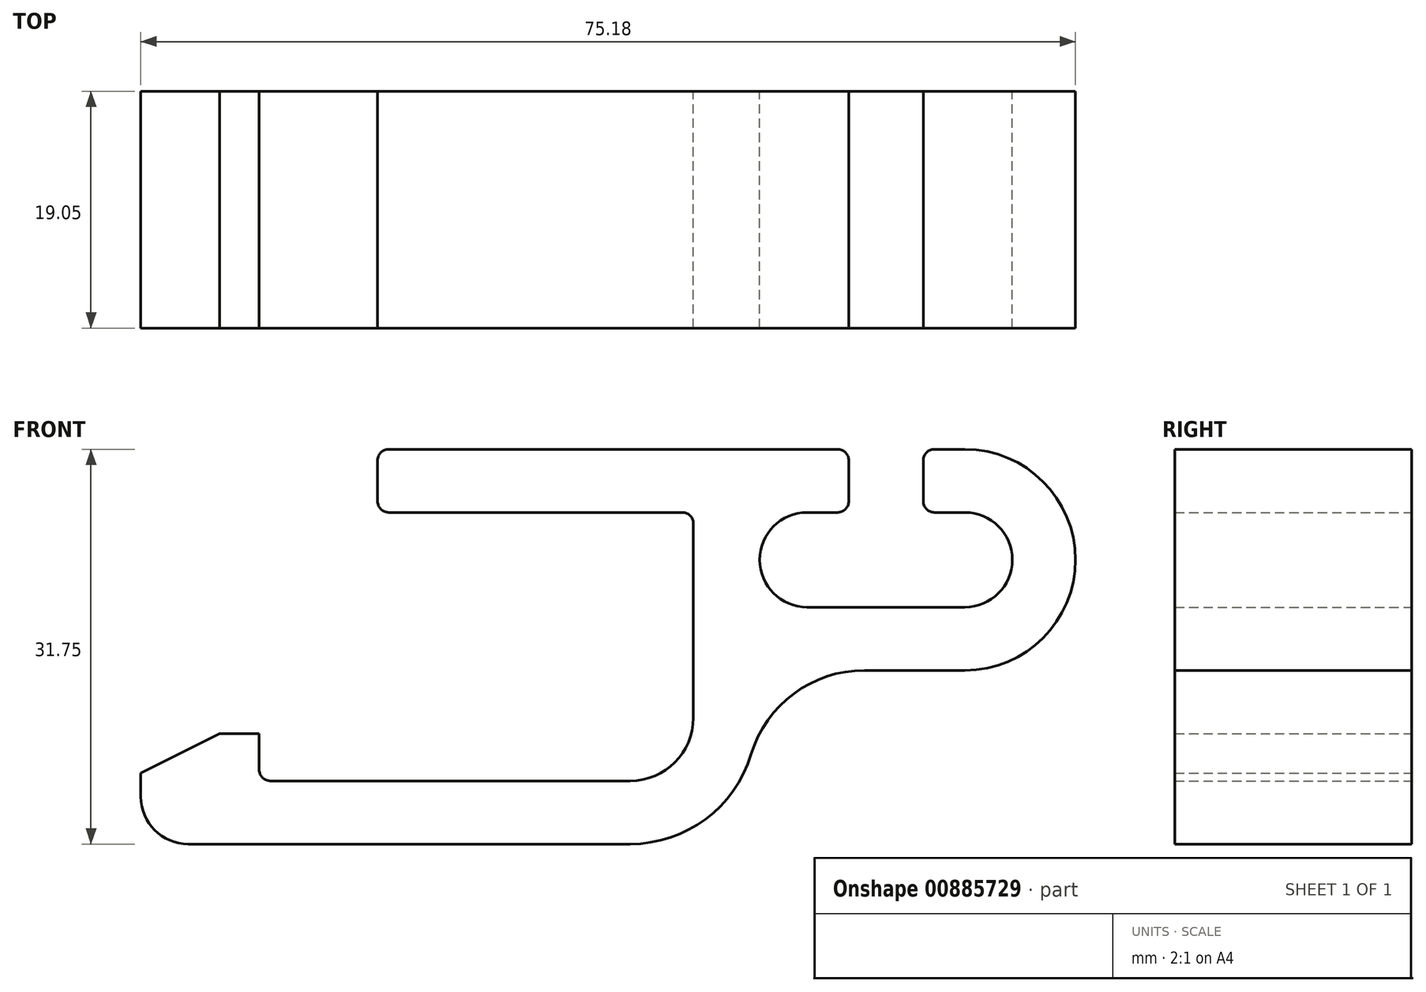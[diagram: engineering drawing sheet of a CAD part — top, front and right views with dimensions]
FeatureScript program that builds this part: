
annotation { "Feature Type Name" : "Feature", "Feature Type Description" : "" }
export const myFeature = defineFeature(function(context is Context, id is Id, definition is map)
    precondition{}
    {
        {
            var Q0;
            Q0=qCreatedBy(makeId("Front.planeOp"),FACE);
            var sketch = newSketch(context, id + "F0", { "sketchPlane" : qUnion([Q0])});
            skLineSegment(sketch, "E0", {"start": v(-0.89, 0) * mm, "end": v(-24.51, 0) * mm});
            skLineSegment(sketch, "E1", {"start": v(-25.4, 0.89) * mm, "end": v(-25.4, 4.2) * mm});
            skLineSegment(sketch, "E2", {"start": v(-24.51, 5.08) * mm, "end": v(11.6, 5.08) * mm});
            skLineSegment(sketch, "E3", {"start": v(-5.08, -26.67) * mm, "end": v(-40.64, -26.67) * mm});
            skLineSegment(sketch, "E4", {"start": v(-44.45, -22.86) * mm, "end": v(-44.45, -20.96) * mm});
            skLineSegment(sketch, "E5", {"start": v(-38.1, -17.78) * mm, "end": v(-34.93, -17.78) * mm});
            skLineSegment(sketch, "E6", {"start": v(-34.93, -17.78) * mm, "end": v(-34.93, -20.7) * mm});
            skLineSegment(sketch, "E7", {"start": v(-34.04, -21.59) * mm, "end": v(-5.08, -21.59) * mm});
            skLineSegment(sketch, "E8", {"start": v(0, -16.51) * mm, "end": v(0, -0.89) * mm});
            skPoint(sketch, "E9.visualSharp", {"position": v(5.08, -26.67) * mm});
            skArc(sketch, "E9.filletArc", {"start": v(-5.08, -26.67) * mm, "mid": v(0.97, -24.67) * mm, "end": v(4.64, -19.46) * mm});
            skPoint(sketch, "E10.visualSharp", {"position": v(0, -21.59) * mm});
            skArc(sketch, "E10.filletArc", {"start": v(-5.08, -21.59) * mm, "mid": v(-1.49, -20.1) * mm, "end": v(0, -16.51) * mm});
            skPoint(sketch, "E11.visualSharp", {"position": v(0, 0) * mm});
            skArc(sketch, "E11.filletArc", {"start": v(0, -0.89) * mm, "mid": v(-0.26, -0.26) * mm, "end": v(-0.89, 0) * mm});
            skPoint(sketch, "E12.visualSharp", {"position": v(-34.93, -21.59) * mm});
            skArc(sketch, "E12.filletArc", {"start": v(-34.93, -20.7) * mm, "mid": v(-34.66, -21.33) * mm, "end": v(-34.04, -21.59) * mm});
            skPoint(sketch, "E13.visualSharp", {"position": v(-44.45, -26.67) * mm});
            skArc(sketch, "E13.filletArc", {"start": v(-44.45, -22.86) * mm, "mid": v(-43.33, -25.55) * mm, "end": v(-40.64, -26.67) * mm});
            skLineSegment(sketch, "E14", {"start": v(-38.1, -17.78) * mm, "end": v(-44.45, -20.96) * mm});
            skPoint(sketch, "E15.visualSharp", {"position": v(-25.4, 0) * mm});
            skArc(sketch, "E15.filletArc", {"start": v(-25.4, 0.89) * mm, "mid": v(-25.14, 0.26) * mm, "end": v(-24.51, 0) * mm});
            skPoint(sketch, "E16.visualSharp", {"position": v(-25.4, 5.08) * mm});
            skArc(sketch, "E16.filletArc", {"start": v(-24.51, 5.08) * mm, "mid": v(-25.14, 4.82) * mm, "end": v(-25.4, 4.2) * mm});
            skLineSegment(sketch, "E17", {"start": v(13.76, -12.7) * mm, "end": v(21.84, -12.7) * mm});
            skLineSegment(sketch, "E18", {"start": v(9.14, -7.62) * mm, "end": v(21.84, -7.62) * mm});
            skLineSegment(sketch, "E19", {"start": v(21.84, 0) * mm, "end": v(19.38, 0) * mm});
            skLineSegment(sketch, "E20", {"start": v(18.5, 0.89) * mm, "end": v(18.5, 4.2) * mm});
            skLineSegment(sketch, "E21", {"start": v(19.38, 5.08) * mm, "end": v(21.84, 5.08) * mm});
            skLineSegment(sketch, "E22", {"start": v(12.5, 0.89) * mm, "end": v(12.5, 4.2) * mm});
            skLineSegment(sketch, "E23", {"start": v(11.6, 0) * mm, "end": v(9.14, 0) * mm});
            skArc(sketch, "E24", {"start": v(9.14, 0) * mm, "mid": v(5.33, -3.8) * mm, "end": v(9.14, -7.62) * mm});
            skArc(sketch, "E25", {"start": v(21.84, 0) * mm, "mid": v(25.65, -3.8) * mm, "end": v(21.84, -7.62) * mm});
            skArc(sketch, "E26", {"start": v(21.84, 5.08) * mm, "mid": v(30.73, -3.8) * mm, "end": v(21.84, -12.7) * mm});
            skPoint(sketch, "E27.visualSharp", {"position": v(4.34, -12.7) * mm});
            skArc(sketch, "E27.filletArc", {"start": v(13.76, -12.7) * mm, "mid": v(8.08, -14.57) * mm, "end": v(4.64, -19.46) * mm});
            skPoint(sketch, "E28.visualSharp", {"position": v(12.5, 0) * mm});
            skArc(sketch, "E28.filletArc", {"start": v(11.6, 0) * mm, "mid": v(12.23, 0.26) * mm, "end": v(12.5, 0.89) * mm});
            skPoint(sketch, "E29.visualSharp", {"position": v(12.5, 5.08) * mm});
            skArc(sketch, "E29.filletArc", {"start": v(12.5, 4.2) * mm, "mid": v(12.23, 4.82) * mm, "end": v(11.6, 5.08) * mm});
            skPoint(sketch, "E30.visualSharp", {"position": v(18.5, 5.08) * mm});
            skArc(sketch, "E30.filletArc", {"start": v(19.38, 5.08) * mm, "mid": v(18.75, 4.82) * mm, "end": v(18.5, 4.2) * mm});
            skPoint(sketch, "E31.visualSharp", {"position": v(18.5, 0) * mm});
            skArc(sketch, "E31.filletArc", {"start": v(18.5, 0.89) * mm, "mid": v(18.75, 0.26) * mm, "end": v(19.38, 0) * mm});
            skSolve(sketch);
        }
        {
            var Q0;
            Q0 = qSketchRegion(id + "F0", true);
            extrude(context, id + "F1", {"entities" : qUnion([Q0]), "depth" : 19.05 * mm, "offsetDistance" : 25.4 * mm});
        }
    });
